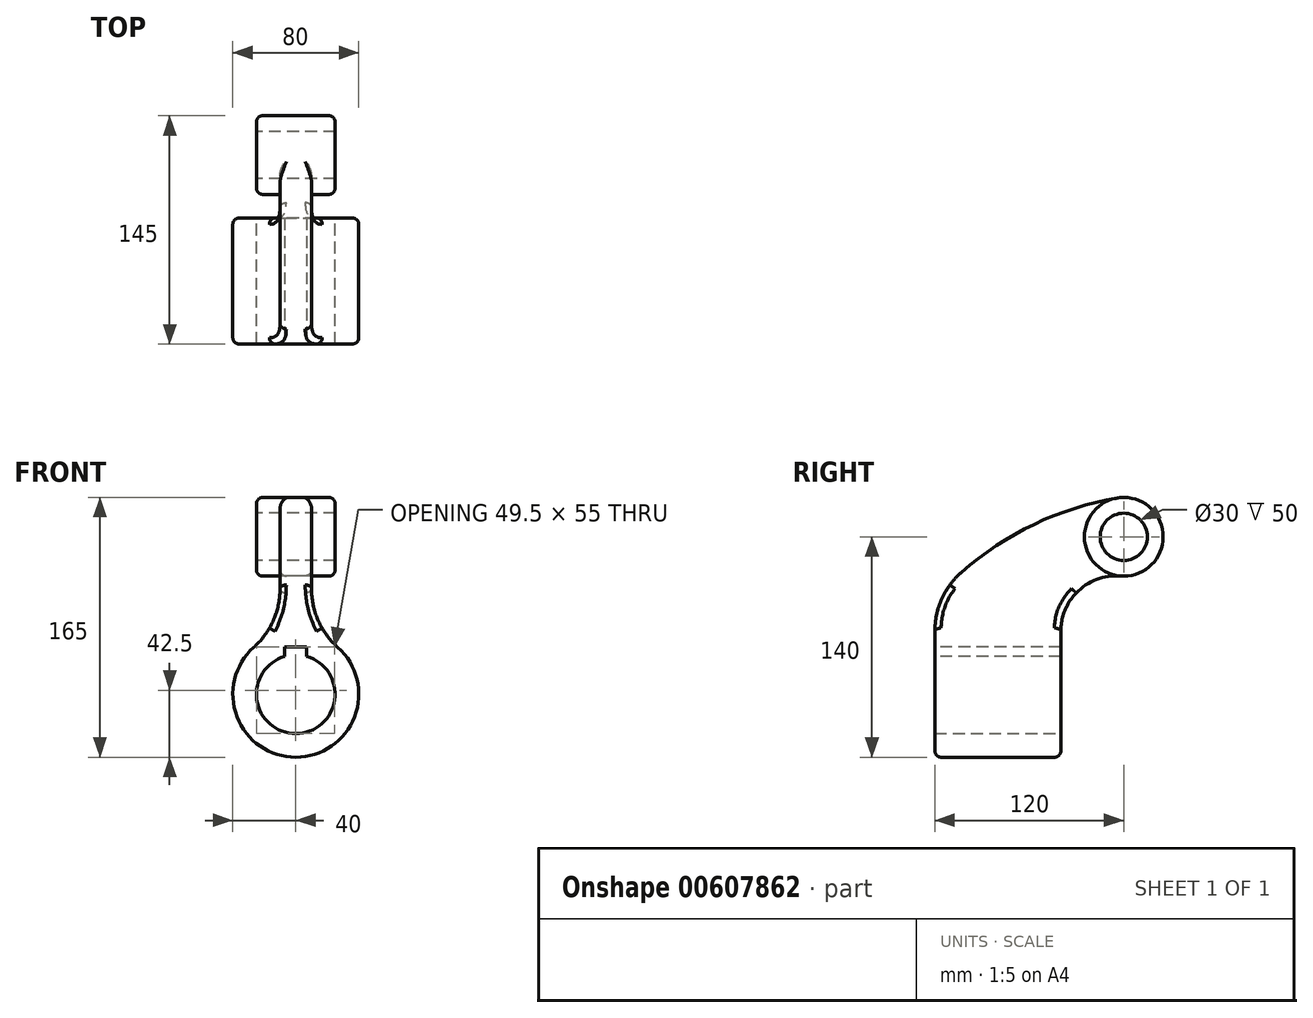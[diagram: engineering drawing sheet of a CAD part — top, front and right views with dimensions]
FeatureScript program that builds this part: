
annotation { "Feature Type Name" : "Feature", "Feature Type Description" : "" }
export const myFeature = defineFeature(function(context is Context, id is Id, definition is map)
    precondition{}
    {
        {
            var Q0;
            Q0=qCreatedBy(makeId("Right.planeOp"),FACE);
            var sketch = newSketch(context, id + "F0", { "sketchPlane" : qUnion([Q0])});
            skLineSegment(sketch, "E0.bottom", {"start": v(0, 25) * mm, "end": v(-80, 25) * mm});
            skLineSegment(sketch, "E0.top", {"start": v(0, 40) * mm, "end": v(-80, 40) * mm});
            skLineSegment(sketch, "E0.left", {"start": v(0, 25) * mm, "end": v(0, 40) * mm});
            skLineSegment(sketch, "E0.right", {"start": v(-80, 25) * mm, "end": v(-80, 40) * mm});
            skLineSegment(sketch, "E1", {"start": v(0, 0) * mm, "end": v(-86, 0) * mm, "construction": true});
            skCircle(sketch, "E2", {"center": v(40, 100) * mm, "radius": 15 * mm});
            skCircle(sketch, "E3", {"center": v(40, 100) * mm, "radius": 25 * mm});
            skArc(sketch, "E4", {"start": v(38, 75.08) * mm, "mid": v(11.32, 65.86) * mm, "end": v(0, 40) * mm});
            skArc(sketch, "E5", {"start": v(-63.05, 77.52) * mm, "mid": v(-75.57, 60.58) * mm, "end": v(-80, 40) * mm});
            skArc(sketch, "E6", {"start": v(35.84, 124.65) * mm, "mid": v(-16.9, 107.99) * mm, "end": v(-63.05, 77.52) * mm});
            skSolve(sketch);
        }
        {
            var Q0;
            Q0=makeQuery(id+"F0.imprint","IMPRINT",FACE,{"disambiguationData":[TD([[makeQuery(id+"F0.imprint","IMPRINT",EDGE,{"derivedFrom":sQuery(id+"F0.wireOp",EDGE,"E0.bottom")}),-1.0]])]});
            var Q1;
            Q1=sQuery(id+"F0.wireOp",EDGE,"E1");
            revolve(context, id + "F1", {"entities" : qUnion([Q0]), "axis" : qUnion([Q1]), "revolveType" : RevolveType.FULL});
        }
        {
            var Q0;
            Q0=makeQuery(id+"F0.imprint","IMPRINT",FACE,{"disambiguationData":[TD([[makeQuery(id+"F0.imprint","IMPRINT",EDGE,{"derivedFrom":sQuery(id+"F0.wireOp",EDGE,"E0.top")}),-1.0]])]});
            var Q1;
            Q1=makeQuery(id+"F0.imprint","IMPRINT",FACE,{"disambiguationData":[TD([[makeQuery(id+"F0.imprint","IMPRINT",EDGE,{"derivedFrom":sQuery(id+"F0.wireOp",EDGE,"E0.bottom")}),-1.0]])]});
            extrude(context, id + "F2", {"entities" : qUnion([Q0, Q1]), "operationType" : NewBodyOperationType.ADD, "endBound" : BoundingType.SYMMETRIC, "depth" : 20 * mm, "offsetDistance" : 25 * mm});
        }
        {
            var Q0;
            Q0=makeQuery(id+"F0.imprint","IMPRINT",FACE,{"disambiguationData":[TD([[makeQuery(id+"F0.imprint","IMPRINT",EDGE,{"derivedFrom":sQuery(id+"F0.wireOp",EDGE,"E2")}),-1.0]])]});
            extrude(context, id + "F3", {"entities" : qUnion([Q0]), "operationType" : NewBodyOperationType.ADD, "endBound" : BoundingType.SYMMETRIC, "depth" : 50 * mm, "offsetDistance" : 25 * mm});
        }
        {
            var Q0;
            Q0=makeQuery(id+"F2.boolean.opBoolean","INTERSECT",EDGE,{"derivedFrom":[makeQuery(id+"F1.opRevolve","SWEPT_FACE",FACE,{"disambiguationData":[OSD([sQuery(id+"F0.wireOp",EDGE,"E0.top")])]}),makeQuery(id+"F2.opExtrude","CAP_FACE",FACE,{"disambiguationData":[OSD([sQuery(id+"F0.wireOp",EDGE,"E0.bottom"),sQuery(id+"F0.wireOp",EDGE,"E0.left"),sQuery(id+"F0.wireOp",EDGE,"E0.right"),sQuery(id+"F0.wireOp",EDGE,"E3"),sQuery(id+"F0.wireOp",EDGE,"E4"),sQuery(id+"F0.wireOp",EDGE,"E5"),sQuery(id+"F0.wireOp",EDGE,"E6")])],"isStart":false})]});
            var Q1;
            Q1=makeQuery(id+"F2.boolean.opBoolean","INTERSECT",EDGE,{"derivedFrom":[makeQuery(id+"F1.opRevolve","SWEPT_FACE",FACE,{"disambiguationData":[OSD([sQuery(id+"F0.wireOp",EDGE,"E0.top")])]}),makeQuery(id+"F2.opExtrude","CAP_FACE",FACE,{"disambiguationData":[OSD([sQuery(id+"F0.wireOp",EDGE,"E0.bottom"),sQuery(id+"F0.wireOp",EDGE,"E0.left"),sQuery(id+"F0.wireOp",EDGE,"E0.right"),sQuery(id+"F0.wireOp",EDGE,"E3"),sQuery(id+"F0.wireOp",EDGE,"E4"),sQuery(id+"F0.wireOp",EDGE,"E5"),sQuery(id+"F0.wireOp",EDGE,"E6")])],"isStart":true})]});
            fillet(context, id + "F4", {"entities" : qUnion([Q0, Q1]), "radius" : 50 * mm, "tangentPropagation" : true, "allowEdgeOverflow" : false});
        }
        {
            var Q0;
            Q0=makeQuery(id+"F1.opRevolve","SWEPT_EDGE",EDGE,{"disambiguationData":[OSD([sQuery(id+"F0.wireOp",EDGE,"E0.top"),sQuery(id+"F0.wireOp",EDGE,"E0.right"),sQuery(id+"F0.wireOp",EDGE,"E5")])]});
            var Q1;
            Q1=makeQuery(id+"F1.opRevolve","SWEPT_EDGE",EDGE,{"disambiguationData":[OSD([sQuery(id+"F0.wireOp",EDGE,"E0.top"),sQuery(id+"F0.wireOp",EDGE,"E0.left"),sQuery(id+"F0.wireOp",EDGE,"E4")])]});
            var Q2;
            Q2=makeQuery(id+"F3.opExtrude","CAP_EDGE",EDGE,{"disambiguationData":[OSD([sQuery(id+"F0.wireOp",EDGE,"E3")])],"isStart":false});
            var Q3;
            Q3=makeQuery(id+"F3.opExtrude","CAP_EDGE",EDGE,{"disambiguationData":[OSD([sQuery(id+"F0.wireOp",EDGE,"E3")])],"isStart":true});
            var Q4;
            Q4=makeQuery(id+"F2.opExtrude","CAP_EDGE",EDGE,{"disambiguationData":[OSD([sQuery(id+"F0.wireOp",EDGE,"E3")])],"isStart":false});
            var Q5;
            Q5=makeQuery(id+"F2.opExtrude","CAP_EDGE",EDGE,{"disambiguationData":[OSD([sQuery(id+"F0.wireOp",EDGE,"E3")])],"isStart":true});
            fillet(context, id + "F5", {"entities" : qUnion([Q0, Q1, Q2, Q3, Q4, Q5]), "radius" : 4 * mm, "tangentPropagation" : true, "allowEdgeOverflow" : false});
        }
        {
            var Q0;
            {var subQ0=sQuery(id+"F0.wireOp",EDGE,"E0.right");Q0=makeQuery(id+"F2.boolean.opBoolean","MERGE",FACE,{"derivedFrom":[makeQuery(id+"F1.opRevolve","SWEPT_FACE",FACE,{"disambiguationData":[OSD([subQ0])]}),makeQuery(id+"F2.opExtrude","SWEPT_FACE",FACE,{"disambiguationData":[OSD([subQ0])]})]});}
            var sketch = newSketch(context, id + "F6", { "sketchPlane" : qUnion([Q0])});
            skPoint(sketch, "E7.startSnap0", {"position": v(0, 40) * mm});
            skLineSegment(sketch, "E8", {"start": v(0, 30) * mm, "end": v(7, 30) * mm});
            skLineSegment(sketch, "E9", {"start": v(7, 30) * mm, "end": v(7, 16.27) * mm});
            skLineSegment(sketch, "E10", {"start": v(7, 16.27) * mm, "end": v(-7, 16.27) * mm});
            skLineSegment(sketch, "E11", {"start": v(-7, 16.27) * mm, "end": v(-7, 30) * mm});
            skLineSegment(sketch, "E12", {"start": v(-7, 30) * mm, "end": v(0, 30) * mm});
            skSolve(sketch);
        }
        {
            var Q0;
            {var subQ2=sQuery(id+"F6.wireOp",EDGE,"E8");Q0=makeQuery(id+"F6.imprint","IMPRINT",FACE,{"disambiguationData":[TD([[makeQuery(id+"F6.imprint","IMPRINT",EDGE,{"derivedFrom":subQ2}),-1.0]])]});}
            extrude(context, id + "F7", {"entities" : qUnion([Q0]), "operationType" : NewBodyOperationType.REMOVE, "oppositeDirection" : true, "depth" : 80 * mm, "offsetDistance" : 25 * mm});
        }
    });
